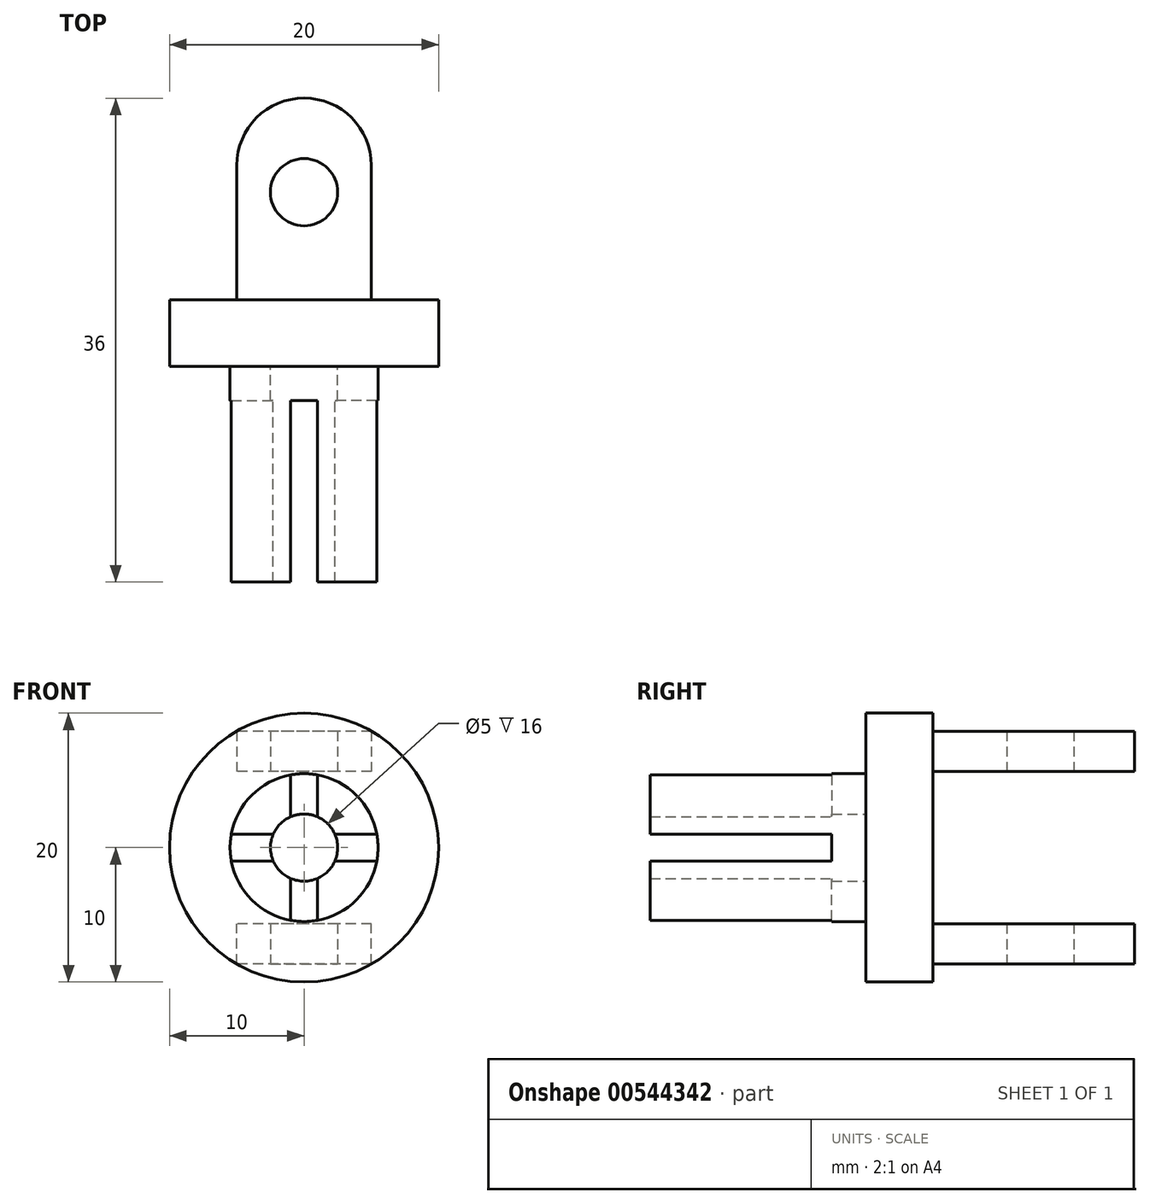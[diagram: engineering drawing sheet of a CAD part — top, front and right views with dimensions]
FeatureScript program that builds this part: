
annotation { "Feature Type Name" : "Feature", "Feature Type Description" : "" }
export const myFeature = defineFeature(function(context is Context, id is Id, definition is map)
    precondition{}
    {
        {
            var Q0;
            Q0=qCreatedBy(makeId("Top.planeOp"),FACE);
            var sketch = newSketch(context, id + "F0", { "sketchPlane" : qUnion([Q0])});
            skLineSegment(sketch, "E0", {"start": v(-10, 6.27) * mm, "end": v(0, 6.27) * mm});
            skLineSegment(sketch, "E1", {"start": v(0, 6.27) * mm, "end": v(0, 1.27) * mm});
            skLineSegment(sketch, "E2", {"start": v(0, 1.27) * mm, "end": v(-2.5, 1.27) * mm});
            skLineSegment(sketch, "E3", {"start": v(-2.5, 1.27) * mm, "end": v(-2.5, -14.73) * mm});
            skLineSegment(sketch, "E4", {"start": v(-2.5, -14.73) * mm, "end": v(-5.5, -14.73) * mm});
            skLineSegment(sketch, "E5", {"start": v(-10, 1.3) * mm, "end": v(-5.5, 1.3) * mm});
            skLineSegment(sketch, "E6", {"start": v(-5.5, 1.3) * mm, "end": v(-5.5, -14.73) * mm});
            skLineSegment(sketch, "E7", {"start": v(-10, 1.3) * mm, "end": v(-10, 6.27) * mm});
            skSolve(sketch);
        }
        {
            var Q0;
            Q0 = qSketchRegion(id + "F0", true);
            var Q1;
            Q1=sQuery(id+"F0.wireOp",EDGE,"E1");
            revolve(context, id + "F1", {"entities" : qUnion([Q0]), "axis" : qUnion([Q1]), "revolveType" : RevolveType.FULL});
        }
        {
            var Q0;
            Q0=makeQuery(id+"F1.opRevolve","SWEPT_FACE",FACE,{"disambiguationData":[OSD([sQuery(id+"F0.wireOp",EDGE,"E0")])]});
            var sketch = newSketch(context, id + "F2", { "sketchPlane" : qUnion([Q0])});
            skLineSegment(sketch, "E8.bottom", {"start": v(-5, 8.66) * mm, "end": v(5, 8.66) * mm});
            skLineSegment(sketch, "E8.top", {"start": v(-5, 5.66) * mm, "end": v(5, 5.66) * mm});
            skLineSegment(sketch, "E8.left", {"start": v(-5, 8.66) * mm, "end": v(-5, 5.66) * mm});
            skLineSegment(sketch, "E8.right", {"start": v(5, 8.66) * mm, "end": v(5, 5.66) * mm});
            skLineSegment(sketch, "E9.bottom", {"start": v(-5, -8.66) * mm, "end": v(5, -8.66) * mm});
            skLineSegment(sketch, "E9.top", {"start": v(-5, -5.66) * mm, "end": v(5, -5.66) * mm});
            skLineSegment(sketch, "E9.left", {"start": v(-5, -8.66) * mm, "end": v(-5, -5.66) * mm});
            skLineSegment(sketch, "E9.right", {"start": v(5, -8.66) * mm, "end": v(5, -5.66) * mm});
            skSolve(sketch);
        }
        {
            var Q0;
            Q0=makeQuery(id+"F2.imprint","IMPRINT",FACE,{"disambiguationData":[TD([[makeQuery(id+"F2.imprint","IMPRINT",EDGE,{"derivedFrom":sQuery(id+"F2.wireOp",EDGE,"E8.bottom")}),-1.0]])]});
            var Q1;
            Q1=makeQuery(id+"F2.imprint","IMPRINT",FACE,{"disambiguationData":[TD([[makeQuery(id+"F2.imprint","IMPRINT",EDGE,{"derivedFrom":sQuery(id+"F2.wireOp",EDGE,"E9.bottom")}),1.0]])]});
            extrude(context, id + "F3", {"entities" : qUnion([Q0, Q1]), "operationType" : NewBodyOperationType.ADD, "depth" : 15 * mm, "offsetDistance" : 25 * mm});
        }
        {
            var Q0;
            Q0=makeQuery(id+"F3.opExtrude","CAP_EDGE",EDGE,{"disambiguationData":[OSD([sQuery(id+"F2.wireOp",EDGE,"E9.right")])],"isStart":false});
            var Q1;
            Q1=makeQuery(id+"F3.opExtrude","CAP_EDGE",EDGE,{"disambiguationData":[OSD([sQuery(id+"F2.wireOp",EDGE,"E9.left")])],"isStart":false});
            var Q2;
            Q2=makeQuery(id+"F3.opExtrude","CAP_EDGE",EDGE,{"disambiguationData":[OSD([sQuery(id+"F2.wireOp",EDGE,"E8.left")])],"isStart":false});
            var Q3;
            Q3=makeQuery(id+"F3.opExtrude","CAP_EDGE",EDGE,{"disambiguationData":[OSD([sQuery(id+"F2.wireOp",EDGE,"E8.right")])],"isStart":false});
            fillet(context, id + "F4", {"entities" : qUnion([Q0, Q1, Q2, Q3]), "radius" : 5 * mm, "tangentPropagation" : true, "allowEdgeOverflow" : false});
        }
        {
            var Q0;
            Q0=makeQuery(id+"F3.opExtrude","SWEPT_FACE",FACE,{"disambiguationData":[OSD([sQuery(id+"F2.wireOp",EDGE,"E9.bottom")])]});
            var sketch = newSketch(context, id + "F5", { "sketchPlane" : qUnion([Q0])});
            skCircle(sketch, "E10", {"center": v(0, -14.27) * mm, "radius": 2.5 * mm});
            skSolve(sketch);
        }
        {
            var Q0;
            Q0=makeQuery(id+"F5.imprint","IMPRINT",FACE,{"disambiguationData":[TD([[makeQuery(id+"F5.imprint","IMPRINT",EDGE,{"derivedFrom":sQuery(id+"F5.wireOp",EDGE,"E10")}),1.0]])]});
            extrude(context, id + "F6", {"entities" : qUnion([Q0]), "operationType" : NewBodyOperationType.REMOVE, "endBound" : BoundingType.THROUGH_ALL, "oppositeDirection" : true, "depth" : 25 * mm, "offsetDistance" : 25 * mm});
        }
        {
            var Q0;
            Q0=makeQuery(id+"F1.opRevolve","SWEPT_FACE",FACE,{"disambiguationData":[OSD([sQuery(id+"F0.wireOp",EDGE,"E4")])]});
            var sketch = newSketch(context, id + "F7", { "sketchPlane" : qUnion([Q0])});
            skLineSegment(sketch, "E11.bottom", {"start": v(-1, 6.22) * mm, "end": v(1, 6.22) * mm});
            skLineSegment(sketch, "E11.top", {"start": v(-1, 1.22) * mm, "end": v(1, 1.22) * mm});
            skLineSegment(sketch, "E11.left", {"start": v(-1, 6.22) * mm, "end": v(-1, 1.22) * mm});
            skLineSegment(sketch, "E11.right", {"start": v(1, 6.22) * mm, "end": v(1, 1.22) * mm});
            skLineSegment(sketch, "E12.1.0", {"start": v(-6.22, -1) * mm, "end": v(-6.22, 1) * mm});
            skLineSegment(sketch, "E12.1.1", {"start": v(-6.22, 1) * mm, "end": v(-1.22, 1) * mm});
            skLineSegment(sketch, "E12.1.2", {"start": v(-6.22, -1) * mm, "end": v(-1.22, -1) * mm});
            skLineSegment(sketch, "E12.1.3", {"start": v(-1.22, -1) * mm, "end": v(-1.22, 1) * mm});
            skLineSegment(sketch, "E12.2.0", {"start": v(1, -6.22) * mm, "end": v(-1, -6.22) * mm});
            skLineSegment(sketch, "E12.2.1", {"start": v(-1, -6.22) * mm, "end": v(-1, -1.22) * mm});
            skLineSegment(sketch, "E12.2.2", {"start": v(1, -6.22) * mm, "end": v(1, -1.22) * mm});
            skLineSegment(sketch, "E12.2.3", {"start": v(1, -1.22) * mm, "end": v(-1, -1.22) * mm});
            skLineSegment(sketch, "E12.3.0", {"start": v(6.22, 1) * mm, "end": v(6.22, -1) * mm});
            skLineSegment(sketch, "E12.3.1", {"start": v(6.22, -1) * mm, "end": v(1.22, -1) * mm});
            skLineSegment(sketch, "E12.3.2", {"start": v(6.22, 1) * mm, "end": v(1.22, 1) * mm});
            skLineSegment(sketch, "E12.3.3", {"start": v(1.22, 1) * mm, "end": v(1.22, -1) * mm});
            skPoint(sketch, "E12.center", {"position": v(0, 0) * mm});
            skSolve(sketch);
        }
        {
            var Q0;
            Q0 = qSketchRegion(id + "F7", true);
            extrude(context, id + "F8", {"entities" : qUnion([Q0]), "operationType" : NewBodyOperationType.REMOVE, "oppositeDirection" : true, "depth" : 13.5 * mm, "offsetDistance" : 25 * mm});
        }
    });
